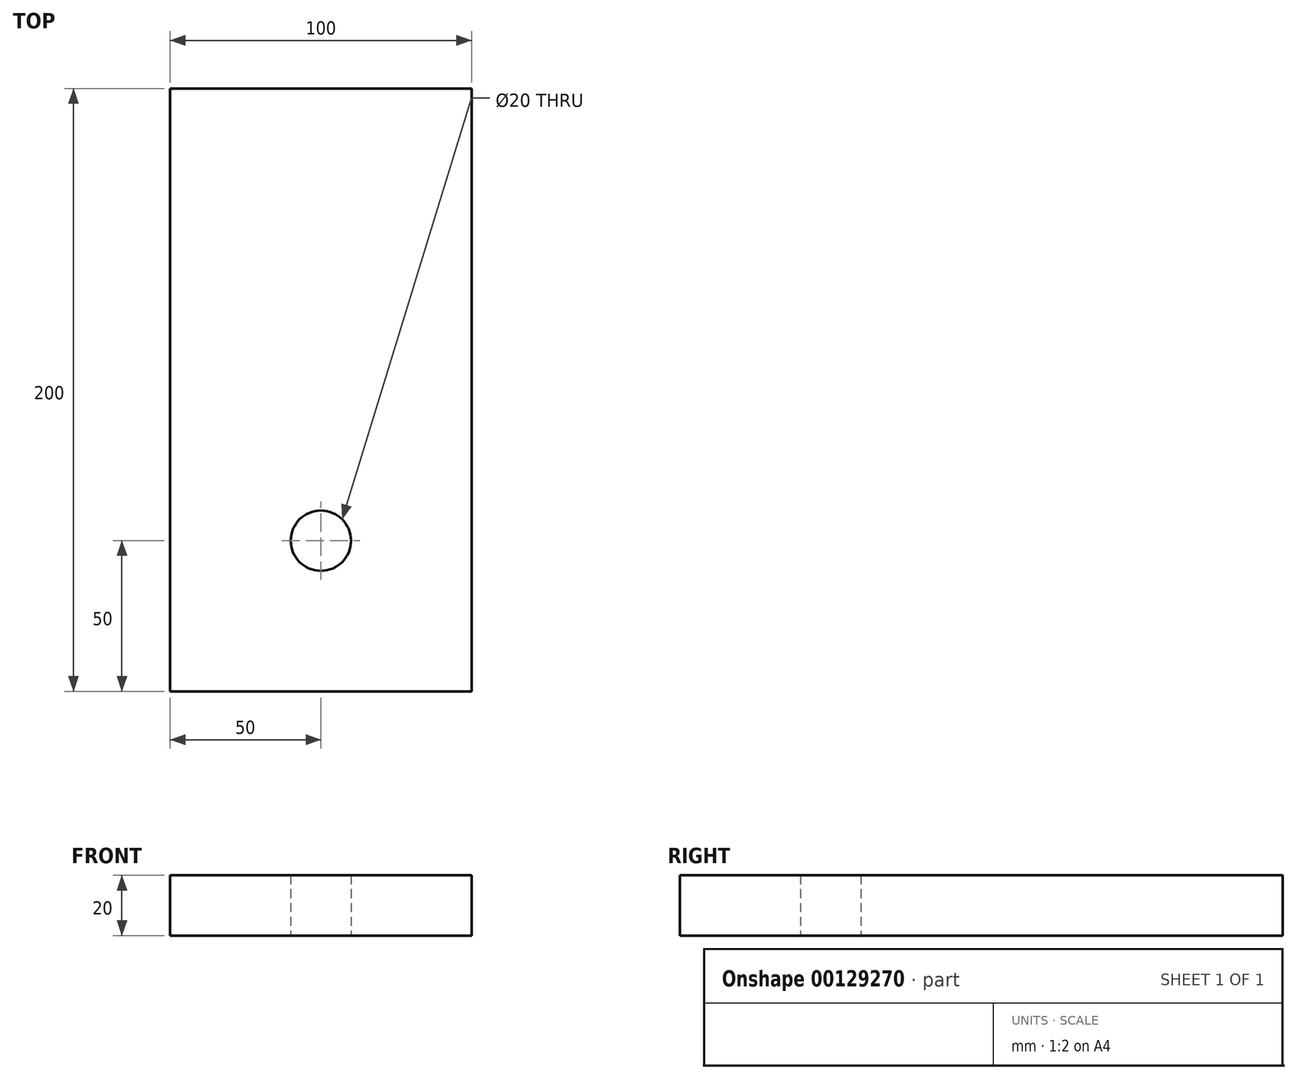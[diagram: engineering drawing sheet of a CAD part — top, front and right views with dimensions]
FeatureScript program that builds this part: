
annotation { "Feature Type Name" : "Feature", "Feature Type Description" : "" }
export const myFeature = defineFeature(function(context is Context, id is Id, definition is map)
    precondition{}
    {
        {
            var Q0;
            Q0=qCreatedBy(makeId("Top.planeOp"),FACE);
            var sketch = newSketch(context, id + "F0", { "sketchPlane" : qUnion([Q0])});
            skLineSegment(sketch, "E0.bottom", {"start": v(0, 0) * mm, "end": v(100, 0) * mm});
            skLineSegment(sketch, "E0.top", {"start": v(0, 200) * mm, "end": v(100, 200) * mm});
            skLineSegment(sketch, "E0.left", {"start": v(0, 0) * mm, "end": v(0, 200) * mm});
            skLineSegment(sketch, "E0.right", {"start": v(100, 0) * mm, "end": v(100, 200) * mm});
            skCircle(sketch, "E1", {"center": v(50, 50) * mm, "radius": 10 * mm});
            skSolve(sketch);
        }
        {
            var Q0;
            Q0=makeQuery(id+"F0.imprint","IMPRINT",FACE,{"disambiguationData":[TD([[makeQuery(id+"F0.imprint","IMPRINT",EDGE,{"derivedFrom":sQuery(id+"F0.wireOp",EDGE,"E0.bottom")}),1.0]])]});
            extrude(context, id + "F1", {"entities" : qUnion([Q0]), "depth" : 20 * mm});
        }
    });
